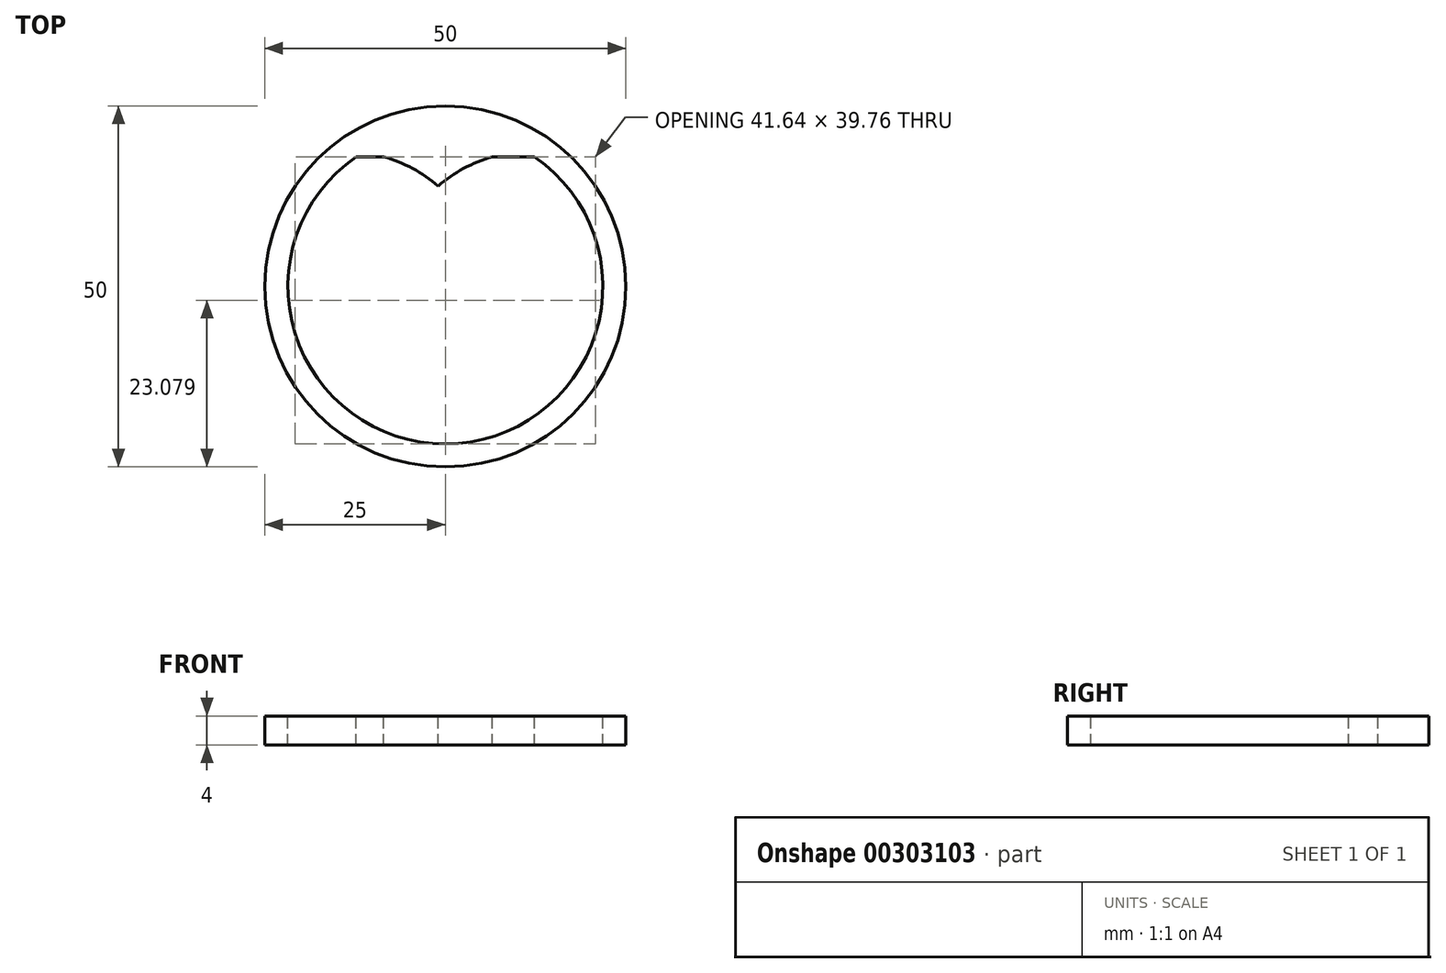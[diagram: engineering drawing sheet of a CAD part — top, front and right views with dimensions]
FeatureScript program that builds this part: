
annotation { "Feature Type Name" : "Feature", "Feature Type Description" : "" }
export const myFeature = defineFeature(function(context is Context, id is Id, definition is map)
    precondition{}
    {
        {
            var Q0;
            Q0=qCreatedBy(makeId("Top.planeOp"),FACE);
            var sketch = newSketch(context, id + "F0", { "sketchPlane" : qUnion([Q0])});
            skCircle(sketch, "E0", {"center": v(0, 0) * mm, "radius": 25 * mm});
            skSolve(sketch);
        }
        {
            var Q0;
            Q0 = qSketchRegion(id + "F0", true);
            extrude(context, id + "F1", {"entities" : qUnion([Q0]), "depth" : 4 * mm});
        }
        {
            var Q0;
            Q0=makeQuery(id+"F1.opExtrude","CAP_FACE",FACE,{"disambiguationData":[OSD([sQuery(id+"F0.wireOp",EDGE,"E0")])],"isStart":false});
            var sketch = newSketch(context, id + "F2", { "sketchPlane" : qUnion([Q0])});
            skCircle(sketch, "E1", {"center": v(0, 0) * mm, "radius": 21.8 * mm});
            skArc(sketch, "E2", {"start": v(-8.52, -10.36) * mm, "mid": v(-6.72, -9.84) * mm, "end": v(-5.04, -9) * mm});
            skArc(sketch, "E3", {"start": v(-8.52, -17.96) * mm, "mid": v(-4.53, -16.36) * mm, "end": v(-1, -13.91) * mm});
            skArc(sketch, "E4.MirrorCS", {"start": v(-8.52, 17.96) * mm, "mid": v(-4.53, 16.36) * mm, "end": v(-1, 13.91) * mm});
            skArc(sketch, "E5.MirrorCS", {"start": v(-8.52, 10.36) * mm, "mid": v(-6.72, 9.84) * mm, "end": v(-5.04, 9) * mm});
            skLineSegment(sketch, "E6", {"start": v(-8.52, 17.96) * mm, "end": v(-12.36, 17.96) * mm});
            skLineSegment(sketch, "E7", {"start": v(-8.52, -17.96) * mm, "end": v(-12.36, -17.96) * mm});
            skLineSegment(sketch, "E8", {"start": v(-10.12, -5.96) * mm, "end": v(-10.12, -10.36) * mm});
            skLineSegment(sketch, "E9", {"start": v(-10.12, -5.96) * mm, "end": v(-10.12, -2.96) * mm});
            skLineSegment(sketch, "E10", {"start": v(-8.52, 10.36) * mm, "end": v(-10.12, 10.36) * mm});
            skLineSegment(sketch, "E11", {"start": v(-8.52, -10.36) * mm, "end": v(-10.12, -10.36) * mm});
            skArc(sketch, "E12.MirrorCS", {"start": v(6.52, 10.36) * mm, "mid": v(4.72, 9.84) * mm, "end": v(3.04, 9) * mm});
            skArc(sketch, "E13.MirrorCS", {"start": v(6.52, -10.36) * mm, "mid": v(4.72, -9.84) * mm, "end": v(3.04, -9) * mm});
            skArc(sketch, "E14.MirrorCS", {"start": v(6.52, 17.96) * mm, "mid": v(2.53, 16.36) * mm, "end": v(-1, 13.91) * mm});
            skArc(sketch, "E15.MirrorCS", {"start": v(6.52, -17.96) * mm, "mid": v(2.53, -16.36) * mm, "end": v(-1, -13.91) * mm});
            skLineSegment(sketch, "E16.MirrorCS", {"start": v(6.52, -17.96) * mm, "end": v(10.36, -17.96) * mm});
            skLineSegment(sketch, "E17.MirrorCS", {"start": v(6.52, -10.36) * mm, "end": v(8.12, -10.36) * mm});
            skLineSegment(sketch, "E18.MirrorCS", {"start": v(6.52, 10.36) * mm, "end": v(8.12, 10.36) * mm});
            skLineSegment(sketch, "E19", {"start": v(10.36, -17.96) * mm, "end": v(12.36, -17.96) * mm});
            skLineSegment(sketch, "E20", {"start": v(6.52, 17.96) * mm, "end": v(12.36, 17.96) * mm});
            skLineSegment(sketch, "E21", {"start": v(15.32, 10.36) * mm, "end": v(15.32, 15.51) * mm});
            skLineSegment(sketch, "E22", {"start": v(-17.32, 3.04) * mm, "end": v(-10.12, 3.04) * mm});
            skLineSegment(sketch, "E23", {"start": v(-17.32, 3.04) * mm, "end": v(-17.32, 10.36) * mm});
            skLineSegment(sketch, "E24", {"start": v(-17.32, -2.96) * mm, "end": v(-10.12, -2.96) * mm});
            skLineSegment(sketch, "E25", {"start": v(-17.32, -5.96) * mm, "end": v(-17.32, -2.96) * mm});
            skLineSegment(sketch, "E26.trimOffspring", {"start": v(-10.12, 3.04) * mm, "end": v(-10.12, 10.36) * mm});
            skLineSegment(sketch, "E27", {"start": v(15.32, -10.36) * mm, "end": v(15.32, -15.51) * mm});
            skLineSegment(sketch, "E28", {"start": v(15.32, 5) * mm, "end": v(8.12, 5) * mm});
            skLineSegment(sketch, "E29", {"start": v(15.32, -5) * mm, "end": v(8.12, -5) * mm});
            skLineSegment(sketch, "E30", {"start": v(15.32, 5) * mm, "end": v(15.32, 10.36) * mm});
            skLineSegment(sketch, "E31", {"start": v(15.32, -5) * mm, "end": v(15.32, -10.36) * mm});
            skLineSegment(sketch, "E32", {"start": v(8.12, 5) * mm, "end": v(8.12, 10.36) * mm});
            skLineSegment(sketch, "E33", {"start": v(8.12, -5) * mm, "end": v(8.12, -10.36) * mm});
            skPoint(sketch, "E34.start.orphan", {"position": v(-1, 0) * mm});
            skPoint(sketch, "E35.orphan", {"position": v(-2, 0) * mm});
            skArc(sketch, "E36.trimOffspring", {"start": v(-1, 4.49) * mm, "mid": v(-1.75, 2.3) * mm, "end": v(-2, 0) * mm});
            skArc(sketch, "E37.trimOffspring", {"start": v(-5.04, 9) * mm, "mid": v(-6.87, 4.66) * mm, "end": v(-7.6, 0) * mm});
            skArc(sketch, "E38.trimOffspring", {"start": v(-1, -4.49) * mm, "mid": v(-1.75, -2.3) * mm, "end": v(-2, 0) * mm});
            skArc(sketch, "E39.trimOffspring", {"start": v(-5.04, -9) * mm, "mid": v(-6.87, -4.66) * mm, "end": v(-7.6, 0) * mm});
            skArc(sketch, "E40.trimOffspring", {"start": v(-1, -4.49) * mm, "mid": v(-0.25, -2.3) * mm, "end": v(0, 0) * mm});
            skArc(sketch, "E41.trimOffspring", {"start": v(3.04, -9) * mm, "mid": v(4.87, -4.66) * mm, "end": v(5.6, 0) * mm});
            skArc(sketch, "E42.trimOffspring", {"start": v(-1, 4.49) * mm, "mid": v(-0.25, 2.3) * mm, "end": v(0, 0) * mm});
            skArc(sketch, "E43.trimOffspring", {"start": v(3.04, 9) * mm, "mid": v(4.87, 4.66) * mm, "end": v(5.6, 0) * mm});
            skLineSegment(sketch, "E44", {"start": v(-17.32, 10.36) * mm, "end": v(-17.32, 13.24) * mm});
            skLineSegment(sketch, "E45", {"start": v(-17.32, -5.96) * mm, "end": v(-17.32, -13.24) * mm});
            skSolve(sketch);
        }
        {
            var Q0;
            Q0=makeQuery(id+"F2.imprint","IMPRINT",FACE,{"disambiguationData":[TD([[makeQuery(id+"F2.imprint","IMPRINT",EDGE,{"derivedFrom":sQuery(id+"F2.wireOp",EDGE,"E2")}),1.0]])]});
            var Q1;
            Q1=makeQuery(id+"F2.imprint","IMPRINT",FACE,{"disambiguationData":[TD([[makeQuery(id+"F2.imprint","IMPRINT",EDGE,{"derivedFrom":sQuery(id+"F2.wireOp",EDGE,"E36.trimOffspring")}),1.0]])]});
            var Q2;
            Q2=makeQuery(id+"F2.imprint","IMPRINT",FACE,{"disambiguationData":[TD([[makeQuery(id+"F2.imprint","IMPRINT",EDGE,{"derivedFrom":sQuery(id+"F2.wireOp",EDGE,"E4.MirrorCS")}),1.0]])]});
            var Q3;
            Q3=makeQuery(id+"F2.imprint","IMPRINT",FACE,{"disambiguationData":[TD([[makeQuery(id+"F2.imprint","IMPRINT",EDGE,{"derivedFrom":sQuery(id+"F2.wireOp",EDGE,"E12.MirrorCS")}),1.0]])]});
            var Q4;
            Q4=makeQuery(id+"F2.imprint","IMPRINT",FACE,{"disambiguationData":[TD([[makeQuery(id+"F2.imprint","IMPRINT",EDGE,{"derivedFrom":sQuery(id+"F2.wireOp",EDGE,"E3")}),-1.0]])]});
            extrude(context, id + "F3", {"entities" : qUnion([Q0, Q1, Q2, Q3, Q4]), "operationType" : NewBodyOperationType.REMOVE, "oppositeDirection" : true, "depth" : 5 * mm});
        }
    });
